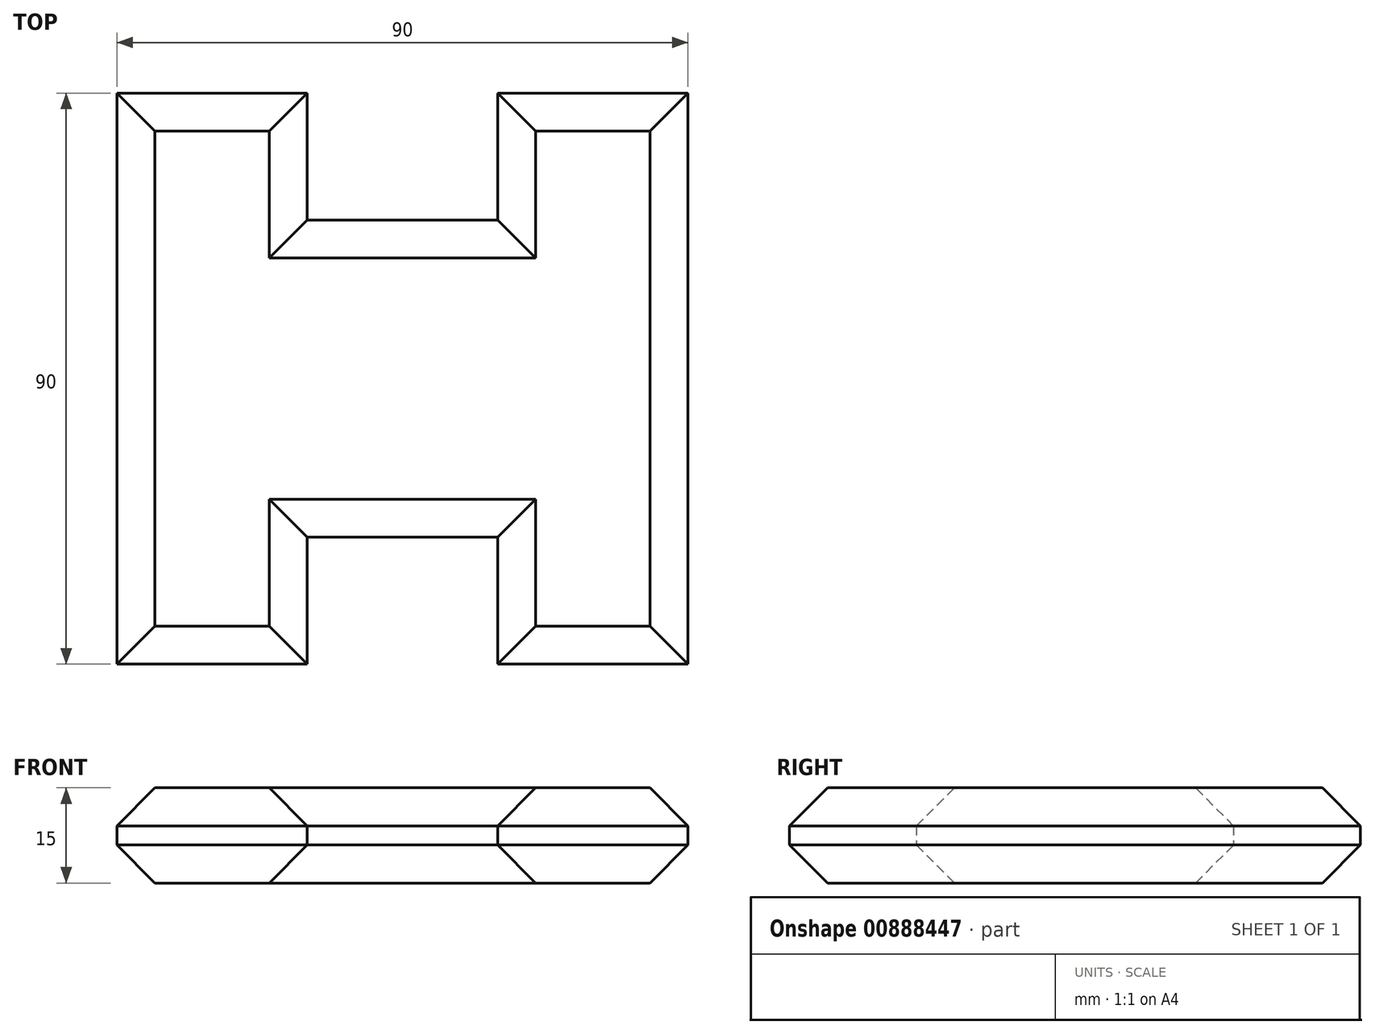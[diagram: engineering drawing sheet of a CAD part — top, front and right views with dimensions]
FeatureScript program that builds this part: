
annotation { "Feature Type Name" : "Feature", "Feature Type Description" : "" }
export const myFeature = defineFeature(function(context is Context, id is Id, definition is map)
    precondition{}
    {
        {
            var Q0;
            Q0=qCreatedBy(makeId("Top.planeOp"),FACE);
            var sketch = newSketch(context, id + "F0", { "sketchPlane" : qUnion([Q0])});
            skLineSegment(sketch, "E0.bottom", {"start": v(45, 25) * mm, "end": v(-45, 25) * mm});
            skLineSegment(sketch, "E0.top", {"start": v(45, -25) * mm, "end": v(-45, -25) * mm});
            skLineSegment(sketch, "E0.left", {"start": v(45, 25) * mm, "end": v(45, -25) * mm});
            skLineSegment(sketch, "E0.right", {"start": v(-45, 25) * mm, "end": v(-45, -25) * mm});
            skPoint(sketch, "E0.middle", {"position": v(0, 0) * mm});
            skLineSegment(sketch, "E1.bottom", {"start": v(-45, 25) * mm, "end": v(-15, 25) * mm});
            skLineSegment(sketch, "E1.top", {"start": v(-45, 45) * mm, "end": v(-15, 45) * mm});
            skLineSegment(sketch, "E1.left", {"start": v(-45, 25) * mm, "end": v(-45, 45) * mm});
            skLineSegment(sketch, "E1.right", {"start": v(-15, 25) * mm, "end": v(-15, 45) * mm});
            skLineSegment(sketch, "E2.bottom", {"start": v(45, 25) * mm, "end": v(15, 25) * mm});
            skLineSegment(sketch, "E2.top", {"start": v(45, 45) * mm, "end": v(15, 45) * mm});
            skLineSegment(sketch, "E2.left", {"start": v(45, 25) * mm, "end": v(45, 45) * mm});
            skLineSegment(sketch, "E2.right", {"start": v(15, 25) * mm, "end": v(15, 45) * mm});
            skLineSegment(sketch, "E3.bottom", {"start": v(-45, -25) * mm, "end": v(-15, -25) * mm});
            skLineSegment(sketch, "E3.top", {"start": v(-45, -45) * mm, "end": v(-15, -45) * mm});
            skLineSegment(sketch, "E3.left", {"start": v(-45, -25) * mm, "end": v(-45, -45) * mm});
            skLineSegment(sketch, "E3.right", {"start": v(-15, -25) * mm, "end": v(-15, -45) * mm});
            skLineSegment(sketch, "E4.bottom", {"start": v(45, -25) * mm, "end": v(15, -25) * mm});
            skLineSegment(sketch, "E4.top", {"start": v(45, -45) * mm, "end": v(15, -45) * mm});
            skLineSegment(sketch, "E4.left", {"start": v(45, -25) * mm, "end": v(45, -45) * mm});
            skLineSegment(sketch, "E4.right", {"start": v(15, -25) * mm, "end": v(15, -45) * mm});
            skSolve(sketch);
        }
        {
            var Q0;
            Q0=makeQuery(id+"F0.imprint","IMPRINT",FACE,{"disambiguationData":[TD([[makeQuery(id+"F0.imprint","IMPRINT",EDGE,{"derivedFrom":sQuery(id+"F0.wireOp",EDGE,"E1.top")}),-1.0]])]});
            var Q1;
            {var subQ6=sQuery(id+"F0.wireOp",EDGE,"E0.left");Q1=makeQuery(id+"F0.imprint","IMPRINT",FACE,{"disambiguationData":[TD([[makeQuery(id+"F0.imprint","IMPRINT",EDGE,{"derivedFrom":subQ6}),-1.0]])]});}
            var Q2;
            Q2=makeQuery(id+"F0.imprint","IMPRINT",FACE,{"disambiguationData":[TD([[makeQuery(id+"F0.imprint","IMPRINT",EDGE,{"derivedFrom":sQuery(id+"F0.wireOp",EDGE,"E2.top")}),1.0]])]});
            var Q3;
            Q3=makeQuery(id+"F0.imprint","IMPRINT",FACE,{"disambiguationData":[TD([[makeQuery(id+"F0.imprint","IMPRINT",EDGE,{"derivedFrom":sQuery(id+"F0.wireOp",EDGE,"E4.top")}),-1.0]])]});
            var Q4;
            Q4=makeQuery(id+"F0.imprint","IMPRINT",FACE,{"disambiguationData":[TD([[makeQuery(id+"F0.imprint","IMPRINT",EDGE,{"derivedFrom":sQuery(id+"F0.wireOp",EDGE,"E3.top")}),1.0]])]});
            extrude(context, id + "F1", {"entities" : qUnion([Q0, Q1, Q2, Q3, Q4]), "depth" : 15 * mm, "offsetDistance" : 25 * mm});
        }
        {
            var Q0;
            Q0=makeQuery(id+"F1.opExtrude","CAP_FACE",FACE,{"disambiguationData":[OSD([sQuery(id+"F0.wireOp",EDGE,"E0.bottom"),sQuery(id+"F0.wireOp",EDGE,"E0.top"),sQuery(id+"F0.wireOp",EDGE,"E0.left"),sQuery(id+"F0.wireOp",EDGE,"E0.right"),sQuery(id+"F0.wireOp",EDGE,"E1.top"),sQuery(id+"F0.wireOp",EDGE,"E1.left"),sQuery(id+"F0.wireOp",EDGE,"E1.right"),sQuery(id+"F0.wireOp",EDGE,"E2.top"),sQuery(id+"F0.wireOp",EDGE,"E2.left"),sQuery(id+"F0.wireOp",EDGE,"E2.right"),sQuery(id+"F0.wireOp",EDGE,"E3.top"),sQuery(id+"F0.wireOp",EDGE,"E3.left"),sQuery(id+"F0.wireOp",EDGE,"E3.right"),sQuery(id+"F0.wireOp",EDGE,"E4.top"),sQuery(id+"F0.wireOp",EDGE,"E4.left"),sQuery(id+"F0.wireOp",EDGE,"E4.right")])],"isStart":false});
            var Q1;
            Q1=makeQuery(id+"F1.opExtrude","CAP_FACE",FACE,{"disambiguationData":[OSD([sQuery(id+"F0.wireOp",EDGE,"E0.bottom"),sQuery(id+"F0.wireOp",EDGE,"E0.top"),sQuery(id+"F0.wireOp",EDGE,"E0.left"),sQuery(id+"F0.wireOp",EDGE,"E0.right"),sQuery(id+"F0.wireOp",EDGE,"E1.top"),sQuery(id+"F0.wireOp",EDGE,"E1.left"),sQuery(id+"F0.wireOp",EDGE,"E1.right"),sQuery(id+"F0.wireOp",EDGE,"E2.top"),sQuery(id+"F0.wireOp",EDGE,"E2.left"),sQuery(id+"F0.wireOp",EDGE,"E2.right"),sQuery(id+"F0.wireOp",EDGE,"E3.top"),sQuery(id+"F0.wireOp",EDGE,"E3.left"),sQuery(id+"F0.wireOp",EDGE,"E3.right"),sQuery(id+"F0.wireOp",EDGE,"E4.top"),sQuery(id+"F0.wireOp",EDGE,"E4.left"),sQuery(id+"F0.wireOp",EDGE,"E4.right")])],"isStart":true});
            chamfer(context, id + "F2", {"entities" : qUnion([Q0, Q1]), "width" : 6 * mm, "tangentPropagation" : true});
        }
    });
